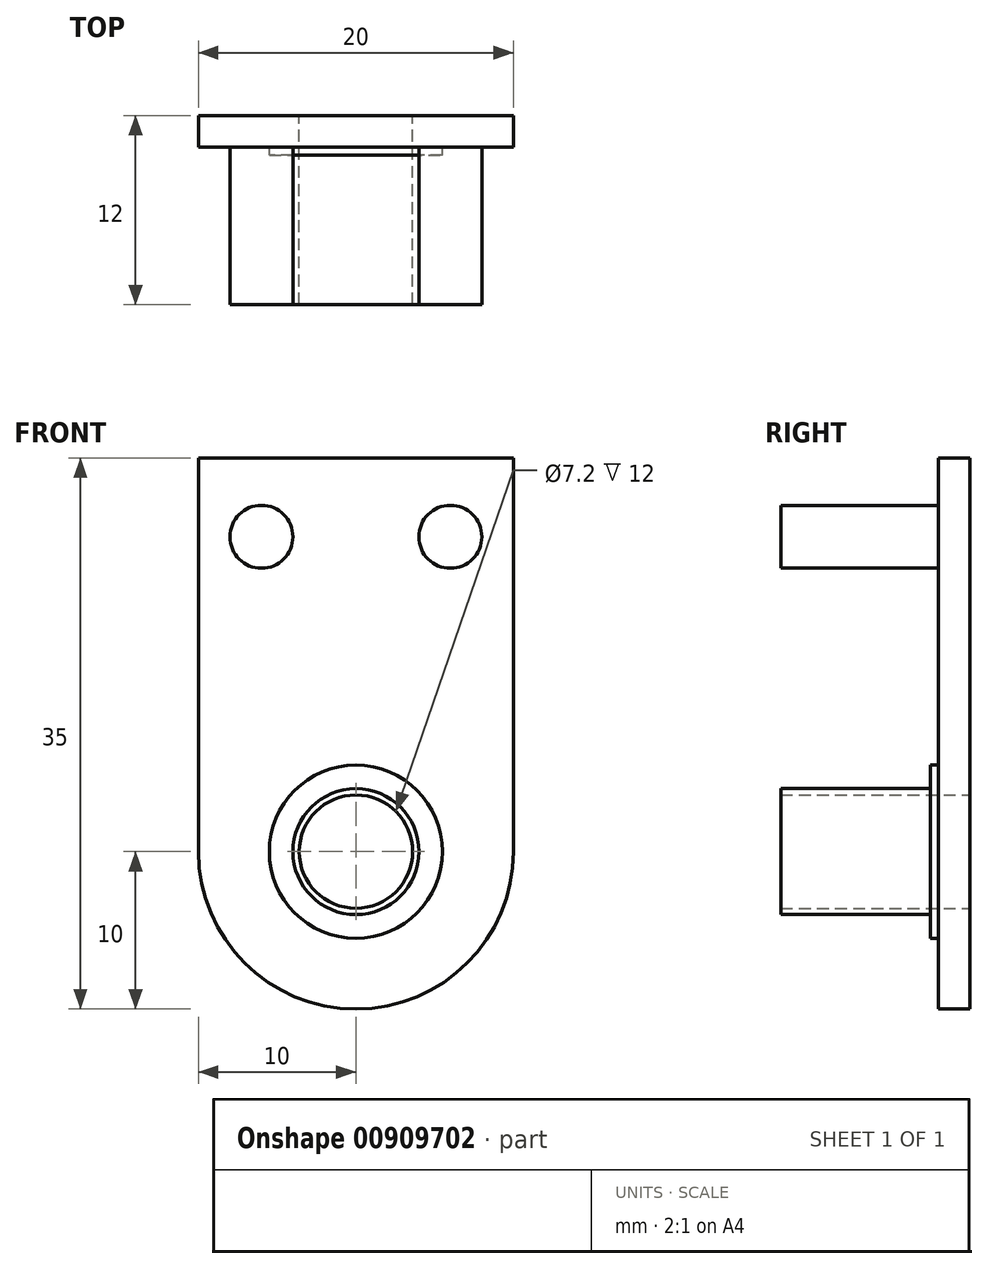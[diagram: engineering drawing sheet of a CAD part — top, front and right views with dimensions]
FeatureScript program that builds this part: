
annotation { "Feature Type Name" : "Feature", "Feature Type Description" : "" }
export const myFeature = defineFeature(function(context is Context, id is Id, definition is map)
    precondition{}
    {
        {
            var Q0;
            Q0=qCreatedBy(makeId("Front.planeOp"),FACE);
            var sketch = newSketch(context, id + "F0", { "sketchPlane" : qUnion([Q0])});
            skPoint(sketch, "E0.middle", {"position": v(0, 0) * mm});
            skCircle(sketch, "E1", {"center": v(0, 0) * mm, "radius": 13 * mm});
            skCircle(sketch, "E2", {"center": v(0, 0) * mm, "radius": 10 * mm});
            skLineSegment(sketch, "E3.bottom", {"start": v(-10, 0) * mm, "end": v(10, 0) * mm});
            skLineSegment(sketch, "E3.top", {"start": v(-10, 25) * mm, "end": v(10, 25) * mm});
            skLineSegment(sketch, "E3.left", {"start": v(-10, 0) * mm, "end": v(-10, 25) * mm});
            skLineSegment(sketch, "E3.right", {"start": v(10, 0) * mm, "end": v(10, 25) * mm});
            skCircle(sketch, "E4", {"center": v(0, 0) * mm, "radius": 3.6 * mm});
            skSolve(sketch);
        }
        {
            var Q0;
            {var subQ5=sQuery(id+"F0.wireOp",EDGE,"E3.top");Q0=makeQuery(id+"F0.imprint","IMPRINT",FACE,{"disambiguationData":[TD([[makeQuery(id+"F0.imprint","IMPRINT",EDGE,{"derivedFrom":subQ5}),-1.0]])]});}
            var Q1;
            {var subQ0=sQuery(id+"F0.wireOp",EDGE,"E3.left");var subQ1=sQuery(id+"F0.wireOp",EDGE,"E1");var subQ2=makeQuery(id+"F0.imprint","INTERSECT",VERTEX,{"derivedFrom":[subQ1,subQ0]});Q1=makeQuery(id+"F0.imprint","IMPRINT",FACE,{"disambiguationData":[TD([[makeQuery(id+"F0.imprint","IMPRINT",EDGE,{"disambiguationData":[TD([[subQ2,1.0]])],"derivedFrom":subQ1}),1.0]])]});}
            var Q2;
            {var subQ0=sQuery(id+"F0.wireOp",EDGE,"E3.bottom");var subQ4=sQuery(id+"F0.wireOp",EDGE,"E4");var subQ5=makeQuery(id+"F0.imprint","INTERSECT",VERTEX,{"disambiguationData":[OD(0.0)],"derivedFrom":[subQ0,subQ4]});Q2=makeQuery(id+"F0.imprint","IMPRINT",FACE,{"disambiguationData":[TD([[makeQuery(id+"F0.imprint","IMPRINT",EDGE,{"disambiguationData":[TD([[subQ5,1.0]])],"derivedFrom":subQ4}),-1.0]])]});}
            var Q3;
            {var subQ0=sQuery(id+"F0.wireOp",EDGE,"E3.bottom");var subQ4=sQuery(id+"F0.wireOp",EDGE,"E4");var subQ5=makeQuery(id+"F0.imprint","INTERSECT",VERTEX,{"disambiguationData":[OD(0.0)],"derivedFrom":[subQ0,subQ4]});Q3=makeQuery(id+"F0.imprint","IMPRINT",FACE,{"disambiguationData":[TD([[makeQuery(id+"F0.imprint","IMPRINT",EDGE,{"disambiguationData":[TD([[subQ5,-1.0]])],"derivedFrom":subQ4}),-1.0]])]});}
            extrude(context, id + "F1", {"entities" : qUnion([Q0, Q1, Q2, Q3]), "depth" : 2 * mm, "offsetDistance" : 25 * mm});
        }
        {
            var Q0;
            Q0=makeQuery(id+"F1.opExtrude","CAP_FACE",FACE,{"disambiguationData":[OSD([sQuery(id+"F0.wireOp",EDGE,"E2"),sQuery(id+"F0.wireOp",EDGE,"E3.top"),sQuery(id+"F0.wireOp",EDGE,"E3.left"),sQuery(id+"F0.wireOp",EDGE,"E3.right"),sQuery(id+"F0.wireOp",EDGE,"E4")])],"isStart":false});
            var sketch = newSketch(context, id + "F2", { "sketchPlane" : qUnion([Q0])});
            skCircle(sketch, "E5", {"center": v(0, 0) * mm, "radius": 4 * mm});
            skCircle(sketch, "E6", {"center": v(0, 0) * mm, "radius": 3.5 * mm});
            skSolve(sketch);
        }
        {
            var Q0;
            Q0=makeQuery(id+"F2.imprint","IMPRINT",FACE,{"disambiguationData":[TD([[makeQuery(id+"F2.imprint","IMPRINT",EDGE,{"derivedFrom":sQuery(id+"F2.wireOp",EDGE,"E5")}),1.0]])]});
            extrude(context, id + "F3", {"entities" : qUnion([Q0]), "operationType" : NewBodyOperationType.ADD, "depth" : 10 * mm, "offsetDistance" : 25 * mm});
        }
        {
            var Q0;
            Q0=makeQuery(id+"F1.opExtrude","CAP_FACE",FACE,{"disambiguationData":[OSD([sQuery(id+"F0.wireOp",EDGE,"E2"),sQuery(id+"F0.wireOp",EDGE,"E3.top"),sQuery(id+"F0.wireOp",EDGE,"E3.left"),sQuery(id+"F0.wireOp",EDGE,"E3.right"),sQuery(id+"F0.wireOp",EDGE,"E4")])],"isStart":false});
            var sketch = newSketch(context, id + "F4", { "sketchPlane" : qUnion([Q0])});
            skCircle(sketch, "E7", {"center": v(-6, 20) * mm, "radius": 2 * mm});
            skCircle(sketch, "E8", {"center": v(6, 20) * mm, "radius": 2 * mm});
            skSolve(sketch);
        }
        {
            var Q0;
            Q0 = qSketchRegion(id + "F4", true);
            extrude(context, id + "F5", {"entities" : qUnion([Q0]), "operationType" : NewBodyOperationType.ADD, "depth" : 10 * mm, "offsetDistance" : 25 * mm});
        }
        {
            var Q0;
            Q0=makeQuery(id+"F1.opExtrude","CAP_FACE",FACE,{"disambiguationData":[OSD([sQuery(id+"F0.wireOp",EDGE,"E2"),sQuery(id+"F0.wireOp",EDGE,"E3.top"),sQuery(id+"F0.wireOp",EDGE,"E3.left"),sQuery(id+"F0.wireOp",EDGE,"E3.right"),sQuery(id+"F0.wireOp",EDGE,"E4")])],"isStart":false});
            var sketch = newSketch(context, id + "F6", { "sketchPlane" : qUnion([Q0])});
            skCircle(sketch, "E9", {"center": v(0, 0) * mm, "radius": 5.5 * mm});
            skCircle(sketch, "E10", {"center": v(0, 0) * mm, "radius": 4 * mm});
            skSolve(sketch);
        }
        {
            var Q0;
            Q0 = qSketchRegion(id + "F6", true);
            extrude(context, id + "F7", {"entities" : qUnion([Q0]), "operationType" : NewBodyOperationType.ADD, "depth" : 0.5 * mm, "offsetDistance" : 25 * mm});
        }
    });
